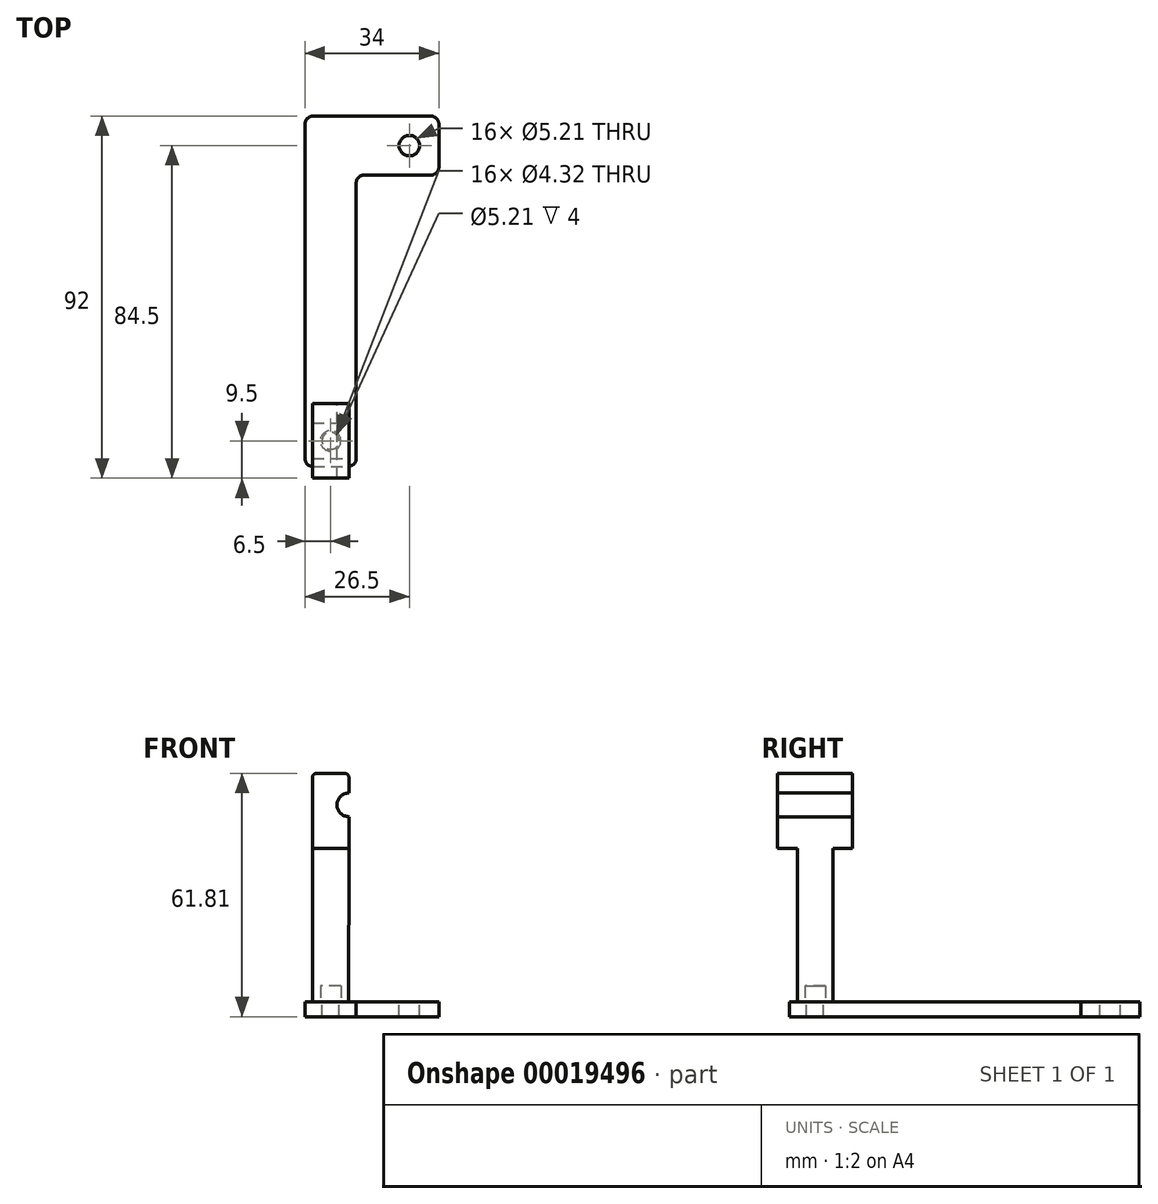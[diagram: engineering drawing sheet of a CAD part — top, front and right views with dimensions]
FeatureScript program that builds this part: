
annotation { "Feature Type Name" : "Feature", "Feature Type Description" : "" }
export const myFeature = defineFeature(function(context is Context, id is Id, definition is map)
    precondition{}
    {
        {
            var Q0;
            Q0=qCreatedBy(makeId("Top.planeOp"),FACE);
            var sketch = newSketch(context, id + "F0", { "sketchPlane" : qUnion([Q0])});
            skLineSegment(sketch, "E0.bottom", {"start": v(-4.5, 82.5) * mm, "end": v(25.5, 82.5) * mm});
            skLineSegment(sketch, "E0.top", {"start": v(-4.5, -6.5) * mm, "end": v(4.5, -6.5) * mm});
            skLineSegment(sketch, "E0.left", {"start": v(-6.5, 80.5) * mm, "end": v(-6.5, -4.5) * mm});
            skLineSegment(sketch, "E0.right", {"start": v(27.5, 80.5) * mm, "end": v(27.5, 69.5) * mm});
            skLineSegment(sketch, "E1.top", {"start": v(8.5, 67.5) * mm, "end": v(25.5, 67.5) * mm});
            skLineSegment(sketch, "E1.left", {"start": v(6.5, -4.5) * mm, "end": v(6.5, 65.5) * mm});
            skPoint(sketch, "E2.visualSharp", {"position": v(-6.5, 82.5) * mm});
            skArc(sketch, "E2.filletArc", {"start": v(-4.5, 82.5) * mm, "mid": v(-5.91, 81.91) * mm, "end": v(-6.5, 80.5) * mm});
            skPoint(sketch, "E3.visualSharp", {"position": v(27.5, 82.5) * mm});
            skArc(sketch, "E3.filletArc", {"start": v(27.5, 80.5) * mm, "mid": v(26.91, 81.91) * mm, "end": v(25.5, 82.5) * mm});
            skPoint(sketch, "E4.visualSharp", {"position": v(27.5, 67.5) * mm});
            skArc(sketch, "E4.filletArc", {"start": v(25.5, 67.5) * mm, "mid": v(26.91, 68.09) * mm, "end": v(27.5, 69.5) * mm});
            skPoint(sketch, "E5.visualSharp", {"position": v(6.5, 67.5) * mm});
            skArc(sketch, "E5.filletArc", {"start": v(8.5, 67.5) * mm, "mid": v(7.09, 66.91) * mm, "end": v(6.5, 65.5) * mm});
            skPoint(sketch, "E6.visualSharp", {"position": v(6.5, -6.5) * mm});
            skArc(sketch, "E6.filletArc", {"start": v(4.5, -6.5) * mm, "mid": v(5.91, -5.91) * mm, "end": v(6.5, -4.5) * mm});
            skPoint(sketch, "E7.visualSharp", {"position": v(-6.5, -6.5) * mm});
            skArc(sketch, "E7.filletArc", {"start": v(-6.5, -4.5) * mm, "mid": v(-5.91, -5.91) * mm, "end": v(-4.5, -6.5) * mm});
            skPoint(sketch, "E8", {"position": v(27.5, 75) * mm});
            skCircle(sketch, "E9", {"center": v(20, 75) * mm, "radius": 2.6 * mm});
            skPoint(sketch, "E10", {"position": v(0, -6.5) * mm});
            skCircle(sketch, "E11", {"center": v(0, 0) * mm, "radius": 2.16 * mm});
            skLineSegment(sketch, "E12", {"start": v(0, 0) * mm, "end": v(0, -6.5) * mm, "construction": true});
            skLineSegment(sketch, "E13", {"start": v(0, 0) * mm, "end": v(6.5, 0) * mm, "construction": true});
            skLineSegment(sketch, "E14", {"start": v(20, 75) * mm, "end": v(27.5, 75) * mm, "construction": true});
            skLineSegment(sketch, "E15", {"start": v(20, 75) * mm, "end": v(20, 82.5) * mm, "construction": true});
            skSolve(sketch);
        }
        {
            var Q0;
            Q0 = qSketchRegion(id + "F0", true);
            extrude(context, id + "F1", {"entities" : qUnion([Q0]), "oppositeDirection" : true, "depth" : 3.8 * mm});
        }
        {
            var Q0;
            Q0=qCreatedBy(makeId("Front.planeOp"),FACE);
            var sketch = newSketch(context, id + "F2", { "sketchPlane" : qUnion([Q0])});
            skLineSegment(sketch, "E16.bottom", {"start": v(-4.6, 0) * mm, "end": v(4.6, 0) * mm});
            skLineSegment(sketch, "E16.right", {"start": v(4.6, 0) * mm, "end": v(4.64, 39) * mm});
            skLineSegment(sketch, "E17", {"start": v(-4.6, 0) * mm, "end": v(-4.6, 39) * mm});
            skLineSegment(sketch, "E18", {"start": v(-3.6, 58) * mm, "end": v(3.64, 58) * mm});
            skLineSegment(sketch, "E19", {"start": v(4.64, 57) * mm, "end": v(4.64, 53) * mm});
            skArc(sketch, "E20", {"start": v(4.64, 53) * mm, "mid": v(1.64, 50) * mm, "end": v(4.64, 47) * mm});
            skPoint(sketch, "E21.visualSharp", {"position": v(-4.6, 58) * mm});
            skArc(sketch, "E21.filletArc", {"start": v(-3.6, 58) * mm, "mid": v(-4.3, 57.7) * mm, "end": v(-4.6, 57) * mm});
            skPoint(sketch, "E22.visualSharp", {"position": v(4.64, 58) * mm});
            skArc(sketch, "E22.filletArc", {"start": v(4.64, 57) * mm, "mid": v(4.35, 57.7) * mm, "end": v(3.64, 58) * mm});
            skLineSegment(sketch, "E23", {"start": v(-4.6, 39) * mm, "end": v(-4.6, 57) * mm});
            skLineSegment(sketch, "E24", {"start": v(4.64, 39) * mm, "end": v(4.64, 47) * mm});
            skLineSegment(sketch, "E25", {"start": v(-4.6, 39) * mm, "end": v(4.64, 39) * mm});
            skSolve(sketch);
        }
        {
            var Q0;
            Q0=qCreatedBy(makeId("Top.planeOp"),FACE);
            var sketch = newSketch(context, id + "F3", { "sketchPlane" : qUnion([Q0])});
            skCircle(sketch, "E26", {"center": v(0, 0) * mm, "radius": 2.6 * mm});
            skSolve(sketch);
        }
        {
            var Q0;
            Q0=makeQuery(id+"F2.imprint","IMPRINT",FACE,{"disambiguationData":[TD([[makeQuery(id+"F2.imprint","IMPRINT",EDGE,{"derivedFrom":sQuery(id+"F2.wireOp",EDGE,"E16.bottom")}),1.0]])]});
            var Q1;
            Q1=makeQuery(id+"F2.imprint","IMPRINT",FACE,{"disambiguationData":[TD([[makeQuery(id+"F2.imprint","IMPRINT",EDGE,{"derivedFrom":sQuery(id+"F2.wireOp",EDGE,"d2720c0f-f27f-49e0-b81f-1f618f3d5b12.bottom")}),1.0]])]});
            extrude(context, id + "F4", {"entities" : qUnion([Q0, Q1]), "endBound" : BoundingType.SYMMETRIC, "depth" : 9 * mm});
        }
        {
            var Q0;
            Q0 = qSketchRegion(id + "F3", true);
            extrude(context, id + "F5", {"entities" : qUnion([Q0]), "operationType" : NewBodyOperationType.REMOVE, "depth" : 4 * mm});
        }
        {
            var Q0;
            Q0=makeQuery(id+"F2.imprint","IMPRINT",FACE,{"disambiguationData":[TD([[makeQuery(id+"F2.imprint","IMPRINT",EDGE,{"derivedFrom":sQuery(id+"F2.wireOp",EDGE,"E18")}),-1.0]])]});
            extrude(context, id + "F6", {"entities" : qUnion([Q0]), "operationType" : NewBodyOperationType.ADD, "endBound" : BoundingType.SYMMETRIC, "depth" : 19 * mm});
        }
    });
